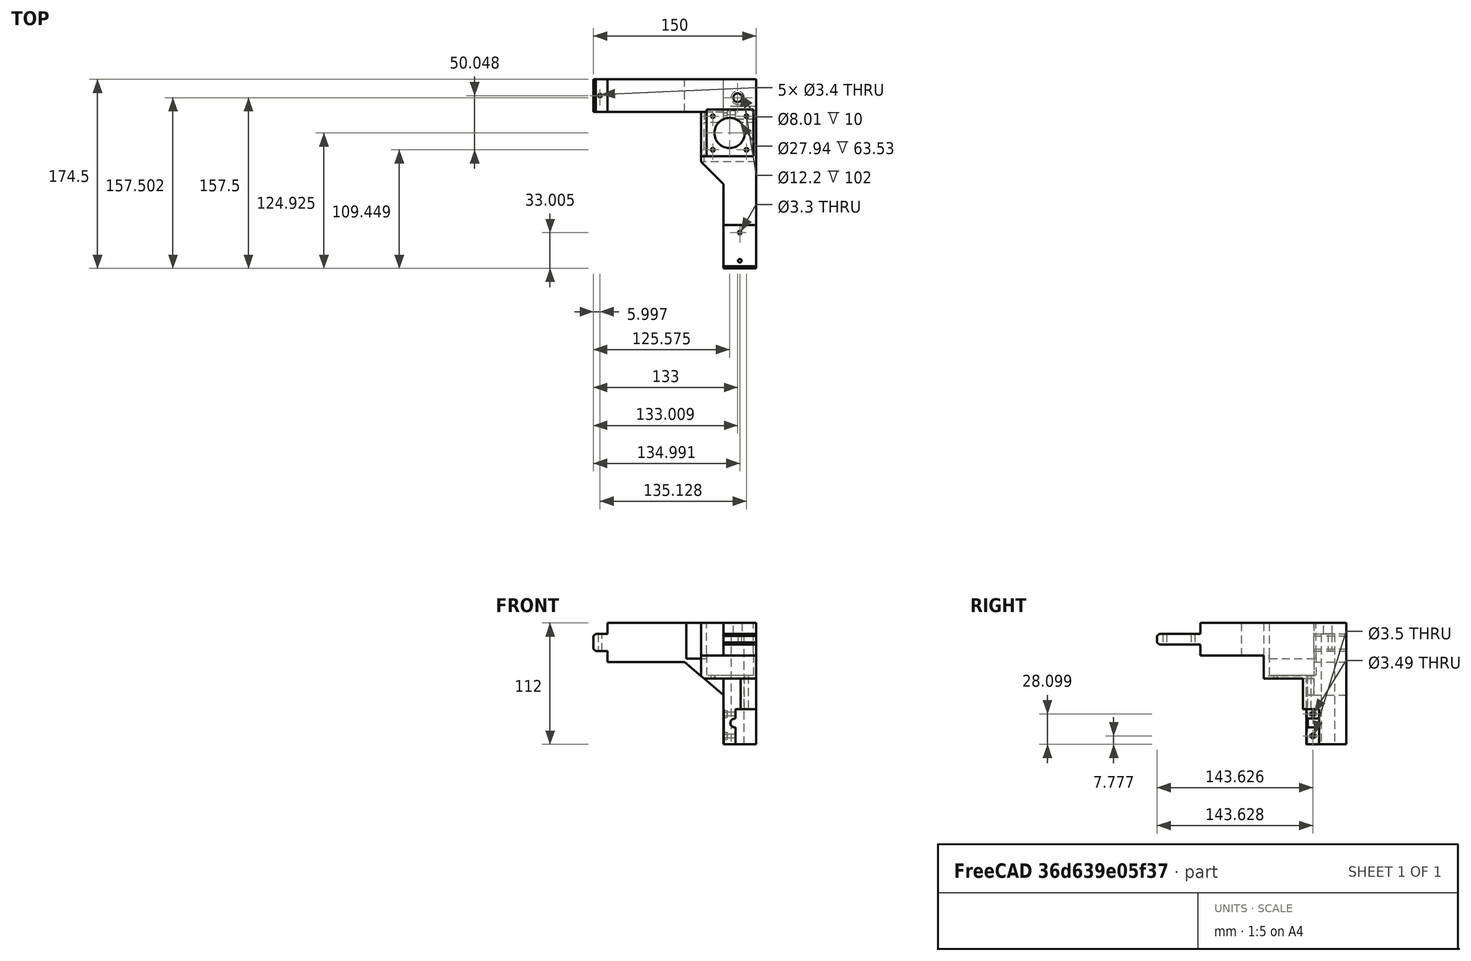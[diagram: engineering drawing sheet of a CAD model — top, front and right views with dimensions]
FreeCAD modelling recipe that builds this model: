
FCSTD DOCUMENT  (FreeCAD 0.21R33668 +26 (Git))
Label: TOP_Right_Rear_Frame
License: All rights reserved
LicenseURL: http://en.wikipedia.org/wiki/All_rights_reserved
objects: PartDesign::Pocket×13, Sketcher::SketchObject×11, Mesh::Feature×1, PartDesign::Pad×1, App::MeasureDistance×1, PartDesign::Chamfer×1, PartDesign::Body×1
note: 42 computed .brp shape members not serialized (recipe doc carries the construction recipe); baked Part::Feature solids carry a one-line shape summary decoded from their .brp

FEATURE [Mesh::Feature] TOP_Right_Rear_Frame
  Placement = pos=(-128.94,0,-140.73) rot=(0,0,1;0rad)
FEATURE [Sketcher::SketchObject] Sketch
  AttachmentOffset = pos=(0,0,-12.5) rot=(0,0,1;0rad)
  FullyConstrained = false
  MapMode = 5
  Placement = pos=(0,12.5,2.8e-15) rot=(1,0,0;1.5708rad)
  Support = -> [XZ_Plane]
  sketch-geometry (11):
    g0: LineSegment StartX=-88.9405 StartY=19.2675 StartZ=0 EndX=-88.9405 EndY=29.2718 EndZ=0
    g1: LineSegment StartX=-88.9405 StartY=29.2718 StartZ=0 EndX=48.0595 EndY=29.2718 EndZ=0
    g2: LineSegment StartX=48.0595 StartY=29.2718 StartZ=0 EndX=48.0595 EndY=-82.73 EndZ=0
    g3: LineSegment StartX=48.0595 StartY=-82.73 StartZ=0 EndX=18.0596 EndY=-82.73 EndZ=0
    g4: LineSegment StartX=18.0596 StartY=-82.73 StartZ=0 EndX=18.0596 EndY=-37.3291 EndZ=0
    g5: LineSegment StartX=18.0596 StartY=-37.3291 StartZ=0 EndX=-17.9125 EndY=-6.73 EndZ=0
    g6: LineSegment StartX=-17.9125 StartY=-6.73 StartZ=0 EndX=-88.9401 EndY=-6.73 EndZ=0
    g7: LineSegment StartX=-88.9405 StartY=19.2675 StartZ=0 EndX=-101.941 EndY=19.2675 EndZ=0
    g8: LineSegment StartX=-88.9401 StartY=-6.73 StartZ=0 EndX=-88.9401 EndY=3.27003 EndZ=0
    g9: LineSegment StartX=-101.941 StartY=19.2675 StartZ=0 EndX=-101.941 EndY=3.27003 EndZ=0
    g10: LineSegment StartX=-101.941 StartY=3.27003 StartZ=0 EndX=-88.9401 EndY=3.27003 EndZ=0
  constraints (25):
    c: Vertical(g0)
    c: Coincident(g0,g1)
    c: Horizontal(g1)
    c: Coincident(g1,g2)
    c: Vertical(g2)
    c: Coincident(g2,g3)
    c: Horizontal(g3)
    c: Coincident(g3,g4)
    c: Vertical(g4)
    c: Coincident(g4,g5)
    c: Coincident(g5,g6)
    c: Horizontal(g6)
    c: Coincident(g7,g0)
    c: Horizontal(g7)
    c: Coincident(g8,g6)
    c: Vertical(g8)
    c: Coincident(g9,g7)
    c: Vertical(g9)
    c: Distance(g1) = 137
    c: DistanceX(g0) = -88.9405
    c: DistanceY(g0) = 29.2718
    c: Distance(g7) = 13
    c: Coincident(g10,g9)
    c: Coincident(g10,g8)
    c: Horizontal(g10)
FEATURE [PartDesign::Pad] Pad
  Direction = (0,-1,2e-16)
  Length = 174.5
  Length2 = 10
  Placement = pos=(0,0,0) rot=(1,0,0;1.5708rad)
  Profile = -> Sketch
  ReferenceAxis = -> Sketch [N_Axis]
  Reversed = true
  Type = 0
FEATURE [Sketcher::SketchObject] Sketch001
  AttachmentOffset = pos=(0,0,39) rot=(0,0,1;0rad)
  FullyConstrained = false
  MapMode = 5
  Placement = pos=(0,0,39) rot=(0,0,1;0rad)
  Support = -> [XY_Plane]
  sketch-geometry (13):
    g0: LineSegment StartX=-128.94 StartY=157 StartZ=0 EndX=-2.61254 EndY=157 EndZ=0
    g1: LineSegment StartX=-2.61254 StartY=157 StartZ=0 EndX=-2.61254 EndY=110.85 EndZ=0
    g2: LineSegment StartX=-2.61254 StartY=110.85 StartZ=0 EndX=-2.60999 EndY=110.85 EndZ=0
    g3: LineSegment StartX=-2.60999 StartY=110.85 StartZ=0 EndX=18.0596 EndY=90.1806 EndZ=0
    g4: LineSegment StartX=18.0596 StartY=90.1806 StartZ=0 EndX=18.0596 EndY=12.5 EndZ=0
    g5: LineSegment StartX=18.0596 StartY=12.5 StartZ=0 EndX=48.06 EndY=12.5 EndZ=0
    g6: LineSegment StartX=48.06 StartY=12.5 StartZ=0 EndX=48.06 EndY=187 EndZ=0
    g7: LineSegment StartX=48.06 StartY=187 StartZ=0 EndX=-128.94 EndY=187 EndZ=0
    g8: LineSegment StartX=-128.94 StartY=187 StartZ=0 EndX=-128.94 EndY=157 EndZ=0
    g9: LineSegment StartX=-215.191 StartY=231.132 StartZ=0 EndX=171.238 EndY=231.132 EndZ=0
    g10: LineSegment StartX=171.238 StartY=231.132 StartZ=0 EndX=171.238 EndY=-46.1665 EndZ=0
    g11: LineSegment StartX=171.238 StartY=-46.1665 StartZ=0 EndX=-215.191 EndY=-46.1665 EndZ=0
    g12: LineSegment StartX=-215.191 StartY=-46.1665 StartZ=0 EndX=-215.191 EndY=231.132 EndZ=0
  constraints (25):
    c: Horizontal(g0)
    c: Coincident(g1,g0)
    c: Vertical(g1)
    c: Coincident(g1,g2)
    c: Horizontal(g2)
    c: Coincident(g2,g3)
    c: Coincident(g3,g4)
    c: Vertical(g4)
    c: Coincident(g4,g5)
    c: Horizontal(g5)
    c: Coincident(g5,g6)
    c: Vertical(g6)
    c: Coincident(g6,g7)
    c: Horizontal(g7)
    c: Coincident(g8,g7)
    c: Coincident(g8,g0)
    c: Vertical(g8)
    c: Coincident(g9,g10)
    c: Coincident(g10,g11)
    c: Coincident(g11,g12)
    c: Coincident(g12,g9)
    c: Horizontal(g9)
    c: Horizontal(g11)
    c: Vertical(g10)
    c: Vertical(g12)
FEATURE [PartDesign::Pocket] Pocket
  BaseFeature = -> Pad
  Direction = (0,0,-1)
  Length = 78
  Length2 = 5
  Placement = pos=(0,0,0) rot=(1,0,0;1.5708rad)
  Profile = -> Sketch001
  ReferenceAxis = -> Sketch001 [N_Axis]
  Type = 0
FEATURE [Sketcher::SketchObject] Sketch002
  AttachmentOffset = pos=(0,0,59) rot=(0,0,1;0rad)
  FullyConstrained = false
  MapMode = 5
  Placement = pos=(59,-1.31e-14,1.31e-14) rot=(0.57735,0.57735,0.57735;2.0944rad)
  Support = -> [YZ_Plane]
  sketch-geometry (20):
    g0: LineSegment StartX=52.5 StartY=19.27 StartZ=0 EndX=12.5 EndY=19.27 EndZ=0
    g1: LineSegment StartX=12.5 StartY=19.27 StartZ=0 EndX=12.5 EndY=9.27 EndZ=0
    g2: LineSegment StartX=12.5 StartY=9.27 StartZ=0 EndX=52.5 EndY=9.27 EndZ=0
    g3: LineSegment StartX=52.5 StartY=9.27 StartZ=0 EndX=52.5 EndY=-0.729993 EndZ=0
    g4: LineSegment StartX=52.5 StartY=-0.729993 StartZ=0 EndX=110.85 EndY=-0.729993 EndZ=0
    g5: LineSegment StartX=110.85 StartY=-0.729993 StartZ=0 EndX=110.85 EndY=-22.03 EndZ=0
    g6: LineSegment StartX=110.85 StartY=-22.03 StartZ=0 EndX=147 EndY=-22.03 EndZ=0
    g7: LineSegment StartX=147 StartY=-22.03 StartZ=0 EndX=147 EndY=-50.23 EndZ=0
    g8: LineSegment StartX=147 StartY=-50.23 StartZ=0 EndX=150.27 EndY=-50.23 EndZ=0
    g9: LineSegment StartX=150.27 StartY=-50.23 StartZ=0 EndX=150.27 EndY=-82.73 EndZ=0
    g10: LineSegment StartX=150.27 StartY=-82.73 StartZ=0 EndX=187 EndY=-82.73 EndZ=0
    g11: LineSegment StartX=187 StartY=-82.73 StartZ=0 EndX=187 EndY=29.27 EndZ=0
    g12: LineSegment StartX=187 StartY=29.27 StartZ=0 EndX=52.5 EndY=29.27 EndZ=0
    g13: LineSegment StartX=52.5 StartY=29.27 StartZ=0 EndX=52.5 EndY=19.27 EndZ=0
    g14: LineSegment StartX=-60.0827 StartY=89.2411 StartZ=0 EndX=285.106 EndY=89.2411 EndZ=0
    g15: LineSegment StartX=285.106 StartY=89.2411 StartZ=0 EndX=285.106 EndY=-150.487 EndZ=0
    g16: LineSegment StartX=285.106 StartY=-150.487 StartZ=0 EndX=-60.0827 EndY=-150.487 EndZ=0
    g17: LineSegment StartX=-60.0827 StartY=-150.487 StartZ=0 EndX=-60.0827 EndY=89.2411 EndZ=0
    g18: Circle CenterX=156.126 CenterY=-54.6313 CenterZ=0 NormalX=0 NormalY=0 NormalZ=1 AngleXU=0 Radius=1.74328
    g19: Circle CenterX=156.128 CenterY=-74.9534 CenterZ=0 NormalX=0 NormalY=0 NormalZ=1 AngleXU=0 Radius=1.75173
  constraints (36):
    c: Horizontal(g0)
    c: Coincident(g0,g1)
    c: Vertical(g1)
    c: Coincident(g1,g2)
    c: Horizontal(g2)
    c: Coincident(g2,g3)
    c: Vertical(g3)
    c: Coincident(g3,g4)
    c: Horizontal(g4)
    c: Coincident(g4,g5)
    c: Vertical(g5)
    c: Coincident(g5,g6)
    c: Horizontal(g6)
    c: Coincident(g6,g7)
    c: Vertical(g7)
    c: Coincident(g7,g8)
    c: Horizontal(g8)
    c: Coincident(g8,g9)
    c: Vertical(g9)
    c: Coincident(g9,g10)
    c: Horizontal(g10)
    c: Coincident(g10,g11)
    c: Vertical(g11)
    c: Coincident(g11,g12)
    c: Horizontal(g12)
    c: Coincident(g12,g13)
    c: Coincident(g13,g0)
    c: Vertical(g13)
    c: Coincident(g14,g15)
    c: Coincident(g15,g16)
    c: Coincident(g16,g17)
    c: Coincident(g17,g14)
    c: Horizontal(g14)
    c: Horizontal(g16)
    c: Vertical(g15)
    c: Vertical(g17)
FEATURE [PartDesign::Pocket] Pocket001
  BaseFeature = -> Pocket
  Direction = (-1,2e-16,-3e-16)
  Length = 123
  Length2 = 75
  Placement = pos=(0,0,0) rot=(1,0,0;1.5708rad)
  Profile = -> Sketch002
  ReferenceAxis = -> Sketch002 [N_Axis]
  Type = 4
FEATURE [PartDesign::Pocket] Pocket002
  BaseFeature = -> Pocket001
  Direction = (-1,2e-16,-3e-16)
  Length = 215
  Length2 = 5
  Placement = pos=(0,0,0) rot=(1,0,0;1.5708rad)
  Profile = -> Sketch002
  ReferenceAxis = -> Sketch002 [N_Axis]
  Type = 0
FEATURE [Sketcher::SketchObject] Sketch003
  AttachmentOffset = pos=(0,0,-162) rot=(0,0,1;0rad)
  FullyConstrained = false
  MapMode = 5
  Placement = pos=(0,162,3.6e-14) rot=(1,0,0;1.5708rad)
  Support = -> [XZ_Plane]
  sketch-geometry (6):
    g0: LineSegment StartX=47.9379 StartY=-50.2448 StartZ=0 EndX=29.0597 EndY=-50.2448 EndZ=0
    g1: LineSegment StartX=29.0597 StartY=-82.9247 StartZ=0 EndX=47.9379 EndY=-82.9247 EndZ=0
    g2: LineSegment StartX=47.9379 StartY=-82.9247 StartZ=0 EndX=47.9379 EndY=-50.2448 EndZ=0
    g3: LineSegment StartX=29.0597 StartY=-50.2448 StartZ=0 EndX=29.0597 EndY=-59.0282 EndZ=0
    g4: LineSegment StartX=29.0597 StartY=-67.1339 StartZ=0 EndX=29.0597 EndY=-82.9247 EndZ=0
    g5: ArcOfCircle CenterX=28.44 CenterY=-63.081 CenterZ=0 NormalX=0 NormalY=0 NormalZ=1 AngleXU=0 Radius=4.09995 StartAngle=1.41906 EndAngle=4.86413
  constraints (11):
    c: Coincident(g0,g3)
    c: Coincident(g4,g1)
    c: Coincident(g1,g2)
    c: Coincident(g2,g0)
    c: Horizontal(g0)
    c: Horizontal(g1)
    c: Vertical(g2)
    c: Vertical(g3)
    c: Vertical(g4)
    c: Coincident(g5,g3)
    c: Coincident(g5,g4)
FEATURE [PartDesign::Pocket] Pocket003
  BaseFeature = -> Pocket002
  Direction = (0,1,2e-16)
  Length = 29
  Length2 = 5
  Placement = pos=(0,0,0) rot=(1,0,0;1.5708rad)
  Profile = -> Sketch003
  ReferenceAxis = -> Sketch003 [N_Axis]
  Reversed = true
  Type = 0
FEATURE [PartDesign::Pocket] Pocket004
  BaseFeature = -> Pocket003
  Direction = (1,0,0)
  Length = 5
  Length2 = 5
  Placement = pos=(0,0,0) rot=(1,0,0;1.5708rad)
  Profile = -> Pocket003 [Face35]
  Type = 0
FEATURE [Sketcher::SketchObject] Sketch004
  AttachmentOffset = pos=(0,0,33) rot=(0,0,1;0rad)
  FullyConstrained = false
  MapMode = 5
  Placement = pos=(0,0,33) rot=(0,0,1;0rad)
  Support = -> [XY_Plane]
  sketch-geometry (6):
    g0: Circle CenterX=31.0691 CenterY=170.002 CenterZ=0 NormalX=0 NormalY=0 NormalZ=1 AngleXU=0 Radius=4.00366
    g1: Circle CenterX=39.1854 CenterY=152.951 CenterZ=0 NormalX=0 NormalY=0 NormalZ=1 AngleXU=0 Radius=1.70042
    g2: Circle CenterX=8.19082 CenterY=152.955 CenterZ=0 NormalX=0 NormalY=0 NormalZ=1 AngleXU=0 Radius=1.70066
    g3: Circle CenterX=8.1899 CenterY=121.949 CenterZ=0 NormalX=0 NormalY=0 NormalZ=1 AngleXU=0 Radius=1.69811
    g4: Circle CenterX=39.183 CenterY=121.95 CenterZ=0 NormalX=0 NormalY=0 NormalZ=1 AngleXU=0 Radius=1.70009
    g5: Circle CenterX=23.635 CenterY=137.425 CenterZ=0 NormalX=0 NormalY=0 NormalZ=1 AngleXU=0 Radius=13.9706
FEATURE [PartDesign::Pocket] Pocket005
  BaseFeature = -> Pocket004
  Direction = (0,0,-1)
  Length = 131
  Length2 = 5
  Placement = pos=(0,0,0) rot=(1,0,0;1.5708rad)
  Profile = -> Sketch004
  ReferenceAxis = -> Sketch004 [N_Axis]
  Type = 0
FEATURE [Sketcher::SketchObject] Sketch005
  FullyConstrained = false
  MapMode = 5
  Placement = pos=(0,0,0) rot=(0.57735,0.57735,0.57735;2.0944rad)
  Support = -> [YZ_Plane]
  sketch-geometry (4):
    g0: LineSegment StartX=146.613 StartY=-22.0985 StartZ=0 EndX=157 EndY=-22.0985 EndZ=0
    g1: LineSegment StartX=157 StartY=-22.0985 StartZ=0 EndX=157 EndY=-37.3303 EndZ=0
    g2: LineSegment StartX=157 StartY=-37.3303 StartZ=0 EndX=146.613 EndY=-37.3303 EndZ=0
    g3: LineSegment StartX=146.613 StartY=-37.3303 StartZ=0 EndX=146.613 EndY=-22.0985 EndZ=0
  constraints (8):
    c: Coincident(g0,g1)
    c: Coincident(g1,g2)
    c: Coincident(g2,g3)
    c: Coincident(g3,g0)
    c: Horizontal(g0)
    c: Horizontal(g2)
    c: Vertical(g1)
    c: Vertical(g3)
FEATURE [PartDesign::Pocket] Pocket006
  BaseFeature = -> Pocket005
  Direction = (-1,2e-16,-3e-16)
  Length = 18.1
  Length2 = 5
  Placement = pos=(0,0,0) rot=(1,0,0;1.5708rad)
  Profile = -> Sketch005
  ReferenceAxis = -> Sketch005 [N_Axis]
  Reversed = true
  Type = 0
FEATURE [Sketcher::SketchObject] Sketch006
  AttachmentOffset = pos=(0,0,1.3) rot=(0,0,1;0rad)
  FullyConstrained = false
  MapMode = 5
  Placement = pos=(0,0,1.3) rot=(0,0,1;0rad)
  Support = -> [XY_Plane]
  sketch-geometry (7):
    g0: LineSegment StartX=-2.61286 StartY=115.95 StartZ=0 EndX=45.5596 EndY=115.95 EndZ=0
    g1: LineSegment StartX=45.5596 StartY=115.95 StartZ=0 EndX=45.5596 EndY=159.111 EndZ=0
    g2: LineSegment StartX=45.5596 StartY=159.111 StartZ=0 EndX=2.38728 EndY=159.111 EndZ=0
    g3: LineSegment StartX=2.38728 StartY=159.111 StartZ=0 EndX=2.38728 EndY=157 EndZ=0
    g4: LineSegment StartX=2.38728 StartY=157 StartZ=0 EndX=-16.3595 EndY=157 EndZ=0
    g5: LineSegment StartX=-16.3595 StartY=157 StartZ=0 EndX=-3.04143 EndY=116.071 EndZ=0
    g6: LineSegment StartX=-3.04143 StartY=116.071 StartZ=0 EndX=-2.61286 EndY=115.95 EndZ=0
  constraints (12):
    c: Horizontal(g0)
    c: Coincident(g1,g0)
    c: Vertical(g1)
    c: Coincident(g2,g1)
    c: Horizontal(g2)
    c: Coincident(g3,g2)
    c: Vertical(g3)
    c: Coincident(g4,g3)
    c: Horizontal(g4)
    c: Coincident(g5,g4)
    c: Coincident(g6,g5)
    c: Coincident(g6,g0)
FEATURE [PartDesign::Pocket] Pocket007
  BaseFeature = -> Pocket006
  Direction = (0,0,-1)
  Length = 44
  Length2 = 5
  Placement = pos=(0,0,0) rot=(1,0,0;1.5708rad)
  Profile = -> Sketch006
  ReferenceAxis = -> Sketch006 [N_Axis]
  Reversed = true
  Type = 0
FEATURE [Sketcher::SketchObject] Sketch007
  FullyConstrained = false
  MapMode = 5
  Support = -> [XY_Plane]
  sketch-geometry (4):
    g0: LineSegment StartX=45.5596 StartY=159.111 StartZ=0 EndX=2.38734 EndY=159.111 EndZ=0
    g1: LineSegment StartX=2.38734 StartY=159.111 StartZ=0 EndX=2.38734 EndY=115.95 EndZ=0
    g2: LineSegment StartX=2.38734 StartY=115.95 StartZ=0 EndX=45.5596 EndY=115.95 EndZ=0
    g3: LineSegment StartX=45.5596 StartY=115.95 StartZ=0 EndX=45.5596 EndY=159.111 EndZ=0
  constraints (8):
    c: Coincident(g0,g1)
    c: Coincident(g1,g2)
    c: Coincident(g2,g3)
    c: Coincident(g3,g0)
    c: Horizontal(g0)
    c: Horizontal(g2)
    c: Vertical(g1)
    c: Vertical(g3)
FEATURE [PartDesign::Pocket] Pocket008
  BaseFeature = -> Pocket007
  Direction = (0,0,-1)
  Length = 19.2
  Length2 = 5
  Placement = pos=(0,0,0) rot=(1,0,0;1.5708rad)
  Profile = -> Sketch007
  ReferenceAxis = -> Sketch007 [N_Axis]
  Type = 0
FEATURE [PartDesign::Pocket] Pocket009
  BaseFeature = -> Pocket008
  Direction = (0,-2e-16,-1)
  Length = 5
  Length2 = 5
  Placement = pos=(0,0,0) rot=(1,0,0;1.5708rad)
  Profile = -> Pocket008 [Face15]
  Type = 0
FEATURE [Sketcher::SketchObject] Sketch008
  AttachmentOffset = pos=(0,0,-85) rot=(0,0,1;0rad)
  FullyConstrained = false
  MapMode = 5
  Placement = pos=(0,0,-85) rot=(0,0,1;0rad)
  Support = -> [XY_Plane]
  sketch-geometry (1):
    g0: Circle CenterX=31.0603 CenterY=170 CenterZ=0 NormalX=0 NormalY=0 NormalZ=1 AngleXU=0 Radius=6.09977
FEATURE [PartDesign::Pocket] Pocket010
  BaseFeature = -> Pocket009
  Direction = (0,0,-1)
  Length = 104.27
  Length2 = 5
  Placement = pos=(0,0,0) rot=(1,0,0;1.5708rad)
  Profile = -> Sketch008
  ReferenceAxis = -> Sketch008 [N_Axis]
  Reversed = true
  Type = 0
FEATURE [Sketcher::SketchObject] Sketch009
  FullyConstrained = false
  MapMode = 5
  Support = -> [XY_Plane]
  sketch-geometry (3):
    g0: Circle CenterX=-95.9429 CenterY=171.998 CenterZ=0 NormalX=0 NormalY=0 NormalZ=1 AngleXU=0 Radius=1.69798
    g1: Circle CenterX=33.0514 CenterY=45.5048 CenterZ=0 NormalX=0 NormalY=0 NormalZ=1 AngleXU=0 Radius=1.64991
    g2: Circle CenterX=33.0661 CenterY=19.498 CenterZ=0 NormalX=0 NormalY=0 NormalZ=1 AngleXU=0 Radius=1.64531
FEATURE [PartDesign::Pocket] Pocket011
  BaseFeature = -> Pocket010
  Direction = (0,0,-1)
  Length = 41
  Length2 = 5
  Placement = pos=(0,0,0) rot=(1,0,0;1.5708rad)
  Profile = -> Sketch009
  ReferenceAxis = -> Sketch009 [N_Axis]
  Reversed = true
  Type = 0
FEATURE [App::MeasureDistance] Distance  label="Distance: 3.29 mm"
  Distance = 3.29236
  P1 = (18.0676,158.936,-53.0226)
  P2 = (21.36,158.937,-53.0238)
FEATURE [Sketcher::SketchObject] Sketch010
  AttachmentOffset = pos=(0,0,18.05) rot=(0,0,1;0rad)
  FullyConstrained = false
  MapMode = 5
  Placement = pos=(18.05,-4e-15,4e-15) rot=(0.57735,0.57735,0.57735;2.0944rad)
  Support = -> [YZ_Plane]
  sketch-geometry (12):
    g0: LineSegment StartX=153.325 StartY=-56.2353 StartZ=0 EndX=156.081 EndY=-57.8858 EndZ=0
    g1: LineSegment StartX=156.081 StartY=-57.8858 StartZ=0 EndX=158.889 EndY=-56.3239 EndZ=0
    g2: LineSegment StartX=158.889 StartY=-56.3239 StartZ=0 EndX=158.94 EndY=-53.1114 EndZ=0
    g3: LineSegment StartX=158.94 StartY=-53.1114 StartZ=0 EndX=156.184 EndY=-51.4609 EndZ=0
    g4: LineSegment StartX=156.184 StartY=-51.4609 StartZ=0 EndX=153.376 EndY=-53.0229 EndZ=0
    g5: LineSegment StartX=153.376 StartY=-53.0229 StartZ=0 EndX=153.325 EndY=-56.2353 EndZ=0
    g6: LineSegment StartX=153.362 StartY=-76.618 StartZ=0 EndX=156.193 EndY=-78.1872 EndZ=0
    g7: LineSegment StartX=156.193 StartY=-78.1872 StartZ=0 EndX=158.968 EndY=-76.5197 EndZ=0
    g8: LineSegment StartX=158.968 StartY=-76.5197 StartZ=0 EndX=158.911 EndY=-73.2831 EndZ=0
    g9: LineSegment StartX=158.911 StartY=-73.2831 StartZ=0 EndX=156.08 EndY=-71.714 EndZ=0
    g10: LineSegment StartX=156.08 StartY=-71.714 StartZ=0 EndX=153.305 EndY=-73.3814 EndZ=0
    g11: LineSegment StartX=153.305 StartY=-73.3814 StartZ=0 EndX=153.362 EndY=-76.618 EndZ=0
  constraints (14):
    c: Coincident(g0,g1)
    c: Coincident(g1,g2)
    c: Coincident(g2,g3)
    c: Coincident(g3,g4)
    c: Coincident(g4,g5)
    c: Coincident(g5,g0)
    c: Equal(g0, g1-g5) x5
    c: Coincident(g6,g7)
    c: Coincident(g7,g8)
    c: Coincident(g8,g9)
    c: Coincident(g9,g10)
    c: Coincident(g10,g11)
    c: Coincident(g11,g6)
    c: Equal(g6, g7-g11) x5
FEATURE [PartDesign::Pocket] Pocket012
  BaseFeature = -> Pocket011
  Direction = (-1,2e-16,-3e-16)
  Length = 3.3
  Length2 = 5
  Placement = pos=(0,0,0) rot=(1,0,0;1.5708rad)
  Profile = -> Sketch010
  ReferenceAxis = -> Sketch010 [N_Axis]
  Reversed = true
  Type = 0
FEATURE [PartDesign::Chamfer] Chamfer
  Angle = 45
  Base = -> Pocket012 [Edge167,Edge170,Edge14,Edge41]
  BaseFeature = -> Pocket012
  ChamferType = 0
  FlipDirection = false
  Placement = pos=(0,0,0) rot=(1,0,0;1.5708rad)
  Size = 2
  Size2 = 1
  SupportTransform = false
  UseAllEdges = false
FEATURE [PartDesign::Body] Body
  Group = -> [Sketch,Pad,Sketch001,Pocket,Sketch002,Pocket001,Pocket002,Sketch003,Pocket003,Pocket004,Sketch004,Pocket005,Sketch005,Pocket006,Sketch006,Pocket007,Sketch007,Pocket008,Pocket009,Sketch008,Pocket010,Sketch009,Pocket011,Sketch010,Pocket012,Chamfer]
  Origin = -> Origin
  Tip = -> Chamfer
